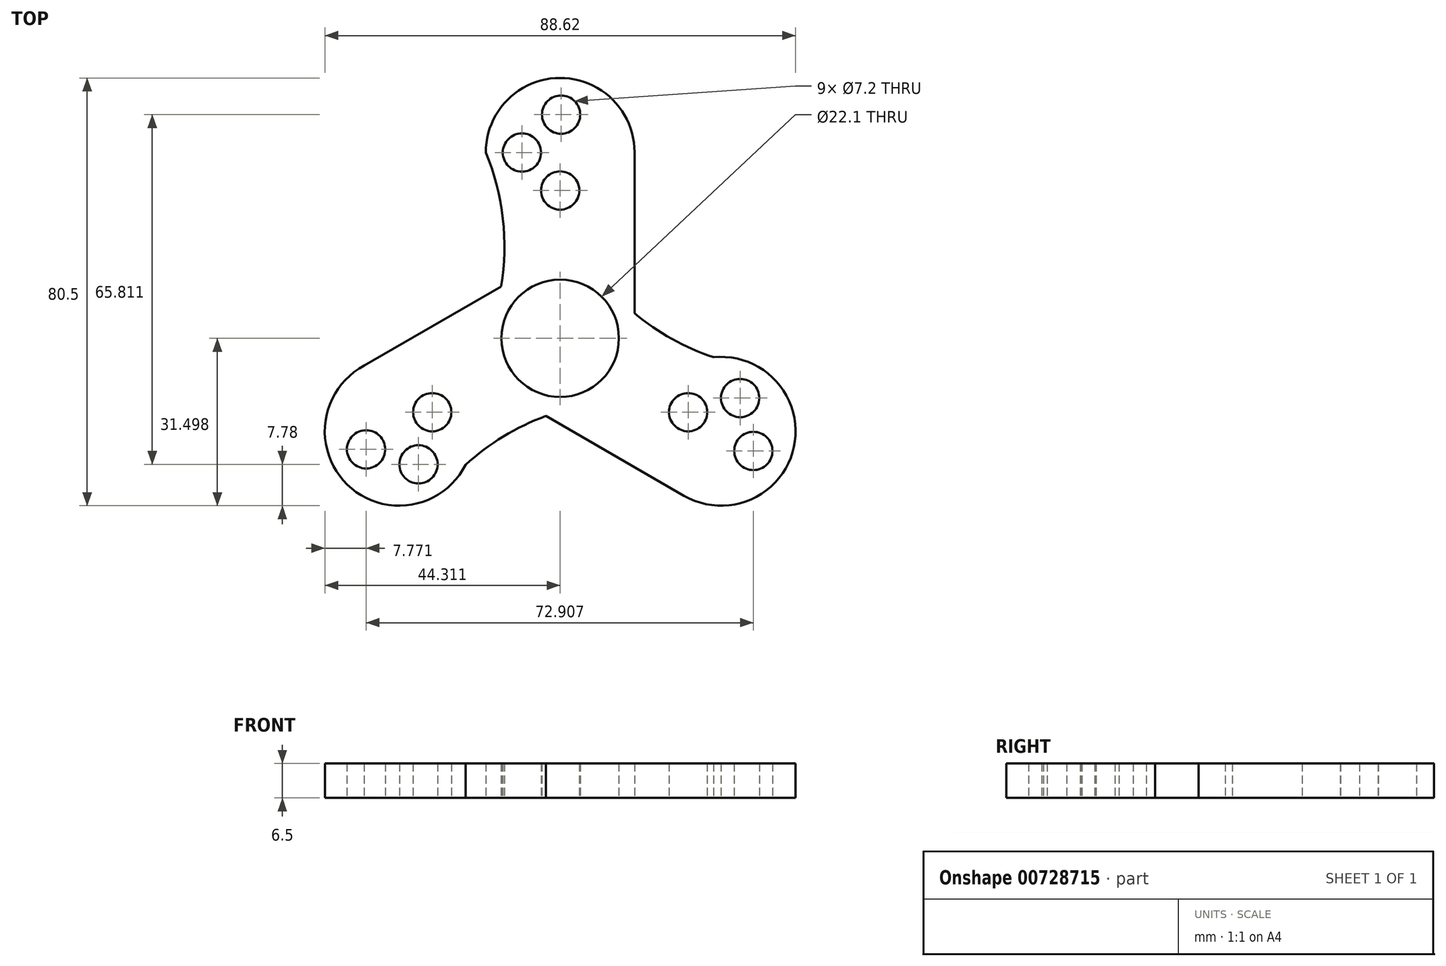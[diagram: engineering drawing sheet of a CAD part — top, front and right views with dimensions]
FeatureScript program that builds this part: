
annotation { "Feature Type Name" : "Feature", "Feature Type Description" : "" }
export const myFeature = defineFeature(function(context is Context, id is Id, definition is map)
    precondition{}
    {
        {
            var Q0;
            Q0=qCreatedBy(makeId("Top.planeOp"),FACE);
            var sketch = newSketch(context, id + "F0", { "sketchPlane" : qUnion([Q0])});
            skCircle(sketch, "E0", {"center": v(0.12, 0.22) * mm, "radius": 11.05 * mm});
            skCircle(sketch, "E1", {"center": v(0.12, 0.22) * mm, "radius": 14 * mm});
            skCircle(sketch, "E2", {"center": v(0.12, 35.22) * mm, "radius": 14 * mm});
            skCircle(sketch, "E3", {"center": v(0.3, 42.31) * mm, "radius": 3.6 * mm});
            skCircle(sketch, "E4", {"center": v(-7.08, 35.18) * mm, "radius": 3.6 * mm});
            skCircle(sketch, "E5.1.0", {"center": v(-30.2, -17.28) * mm, "radius": 14 * mm});
            skCircle(sketch, "E5.2.0", {"center": v(30.43, -17.28) * mm, "radius": 14 * mm});
            skCircle(sketch, "E6.1.0", {"center": v(-36.42, -20.68) * mm, "radius": 3.6 * mm});
            skCircle(sketch, "E6.2.0", {"center": v(36.49, -20.98) * mm, "radius": 3.6 * mm});
            skCircle(sketch, "E7.1.0", {"center": v(-26.55, -23.5) * mm, "radius": 3.6 * mm});
            skCircle(sketch, "E7.2.0", {"center": v(34, -11.02) * mm, "radius": 3.6 * mm});
            skCircle(sketch, "E8", {"center": v(0.12, 28.03) * mm, "radius": 3.6 * mm});
            skCircle(sketch, "E9.1.0", {"center": v(-23.97, -13.69) * mm, "radius": 3.6 * mm});
            skCircle(sketch, "E9.2.0", {"center": v(24.2, -13.69) * mm, "radius": 3.6 * mm});
            skArc(sketch, "E10", {"start": v(-18.8, -9.13) * mm, "mid": v(-10.67, 12.4) * mm, "end": v(-13.88, 35.18) * mm});
            skArc(sketch, "E11.1.0", {"start": v(17.59, -11.72) * mm, "mid": v(-5.12, -15.43) * mm, "end": v(-23.25, -29.6) * mm});
            skArc(sketch, "E11.2.0", {"start": v(1.63, 21.1) * mm, "mid": v(16.2, 3.28) * mm, "end": v(37.54, -5.33) * mm});
            skPoint(sketch, "E11.center", {"position": v(0.14, 0.08) * mm});
            skLineSegment(sketch, "E12", {"start": v(14.12, 35.22) * mm, "end": v(14.12, 0.22) * mm});
            skLineSegment(sketch, "E13.1.0", {"start": v(-37.56, -5.38) * mm, "end": v(-7.25, 12.12) * mm});
            skPoint(sketch, "E13.center", {"position": v(0, 0) * mm});
            skLineSegment(sketch, "E14", {"start": v(-6.58, -12.07) * mm, "end": v(23.43, -29.4) * mm});
            skSolve(sketch);
        }
        {
            var Q0;
            {var subQ0=sQuery(id+"F0.wireOp",EDGE,"E11.1.0");var subQ1=sQuery(id+"F0.wireOp",EDGE,"E5.1.0");var subQ2=makeQuery(id+"F0.imprint","INTERSECT",VERTEX,{"disambiguationData":[OD(0.0)],"derivedFrom":[subQ1,subQ0]});Q0=makeQuery(id+"F0.imprint","IMPRINT",FACE,{"disambiguationData":[TD([[makeQuery(id+"F0.imprint","IMPRINT",EDGE,{"disambiguationData":[TD([[subQ2,-1.0]])],"derivedFrom":subQ1}),1.0]])]});}
            var Q1;
            {var subQ0=sQuery(id+"F0.wireOp",EDGE,"E14");var subQ1=sQuery(id+"F0.wireOp",EDGE,"E1");var subQ2=makeQuery(id+"F0.imprint","INTERSECT",VERTEX,{"derivedFrom":[subQ1,subQ0]});Q1=makeQuery(id+"F0.imprint","IMPRINT",FACE,{"disambiguationData":[TD([[makeQuery(id+"F0.imprint","IMPRINT",EDGE,{"disambiguationData":[TD([[subQ2,-1.0]])],"derivedFrom":subQ1}),-1.0]])]});}
            var Q2;
            {var subQ0=sQuery(id+"F0.wireOp",EDGE,"E11.1.0");var subQ1=sQuery(id+"F0.wireOp",EDGE,"E1");var subQ2=makeQuery(id+"F0.imprint","INTERSECT",VERTEX,{"disambiguationData":[OD(0.0)],"derivedFrom":[subQ1,subQ0]});Q2=makeQuery(id+"F0.imprint","IMPRINT",FACE,{"disambiguationData":[TD([[makeQuery(id+"F0.imprint","IMPRINT",EDGE,{"disambiguationData":[TD([[subQ2,-1.0]])],"derivedFrom":subQ1}),1.0]])]});}
            var Q3;
            Q3=makeQuery(id+"F0.imprint","IMPRINT",FACE,{"disambiguationData":[TD([[makeQuery(id+"F0.imprint","IMPRINT",EDGE,{"derivedFrom":sQuery(id+"F0.wireOp",EDGE,"E6.2.0")}),-1.0]])]});
            var Q4;
            Q4=makeQuery(id+"F0.imprint","IMPRINT",FACE,{"disambiguationData":[TD([[makeQuery(id+"F0.imprint","IMPRINT",EDGE,{"derivedFrom":sQuery(id+"F0.wireOp",EDGE,"E6.1.0")}),-1.0]])]});
            var Q5;
            {var subQ0=sQuery(id+"F0.wireOp",EDGE,"E13.1.0");var subQ1=sQuery(id+"F0.wireOp",EDGE,"E1");var subQ2=makeQuery(id+"F0.imprint","INTERSECT",VERTEX,{"derivedFrom":[subQ1,subQ0]});Q5=makeQuery(id+"F0.imprint","IMPRINT",FACE,{"disambiguationData":[TD([[makeQuery(id+"F0.imprint","IMPRINT",EDGE,{"disambiguationData":[TD([[subQ2,-1.0]])],"derivedFrom":subQ1}),-1.0]])]});}
            var Q6;
            {var subQ0=sQuery(id+"F0.wireOp",EDGE,"E10");var subQ1=sQuery(id+"F0.wireOp",EDGE,"E1");var subQ2=makeQuery(id+"F0.imprint","INTERSECT",VERTEX,{"disambiguationData":[OD(0.0)],"derivedFrom":[subQ1,subQ0]});Q6=makeQuery(id+"F0.imprint","IMPRINT",FACE,{"disambiguationData":[TD([[makeQuery(id+"F0.imprint","IMPRINT",EDGE,{"disambiguationData":[TD([[subQ2,-1.0]])],"derivedFrom":subQ1}),1.0]])]});}
            var Q7;
            {var subQ0=sQuery(id+"F0.wireOp",EDGE,"E11.2.0");var subQ1=sQuery(id+"F0.wireOp",EDGE,"E1");var subQ2=makeQuery(id+"F0.imprint","INTERSECT",VERTEX,{"disambiguationData":[OD(0.0)],"derivedFrom":[subQ1,subQ0]});Q7=makeQuery(id+"F0.imprint","IMPRINT",FACE,{"disambiguationData":[TD([[makeQuery(id+"F0.imprint","IMPRINT",EDGE,{"disambiguationData":[TD([[subQ2,1.0]])],"derivedFrom":subQ1}),1.0]])]});}
            var Q8;
            {var subQ0=sQuery(id+"F0.wireOp",EDGE,"E12");var subQ1=sQuery(id+"F0.wireOp",EDGE,"E1");var subQ2=makeQuery(id+"F0.imprint","INTERSECT",VERTEX,{"derivedFrom":[subQ1,subQ0]});Q8=makeQuery(id+"F0.imprint","IMPRINT",FACE,{"disambiguationData":[TD([[makeQuery(id+"F0.imprint","IMPRINT",EDGE,{"disambiguationData":[TD([[subQ2,-1.0]])],"derivedFrom":subQ1}),-1.0]])]});}
            var Q9;
            {var subQ0=sQuery(id+"F0.wireOp",EDGE,"E10");var subQ1=sQuery(id+"F0.wireOp",EDGE,"E2");var subQ2=makeQuery(id+"F0.imprint","INTERSECT",VERTEX,{"disambiguationData":[OD(0.0)],"derivedFrom":[subQ1,subQ0]});Q9=makeQuery(id+"F0.imprint","IMPRINT",FACE,{"disambiguationData":[TD([[makeQuery(id+"F0.imprint","IMPRINT",EDGE,{"disambiguationData":[TD([[subQ2,-1.0]])],"derivedFrom":subQ1}),1.0]])]});}
            var Q10;
            Q10=makeQuery(id+"F0.imprint","IMPRINT",FACE,{"disambiguationData":[TD([[makeQuery(id+"F0.imprint","IMPRINT",EDGE,{"derivedFrom":sQuery(id+"F0.wireOp",EDGE,"599df940-7847-41b0-ac96-d3a5cff95a5d")}),-1.0]])]});
            var Q11;
            {var subQ5=sQuery(id+"F0.wireOp",EDGE,"E11.2.0");var subQ6=sQuery(id+"F0.wireOp",EDGE,"E1");var subQ7=makeQuery(id+"F0.imprint","INTERSECT",VERTEX,{"disambiguationData":[OD(0.0)],"derivedFrom":[subQ6,subQ5]});Q11=makeQuery(id+"F0.imprint","IMPRINT",FACE,{"disambiguationData":[TD([[makeQuery(id+"F0.imprint","IMPRINT",EDGE,{"disambiguationData":[TD([[subQ7,1.0]])],"derivedFrom":subQ6}),-1.0]])]});}
            var Q12;
            Q12=makeQuery(id+"F0.imprint","IMPRINT",FACE,{"disambiguationData":[TD([[makeQuery(id+"F0.imprint","IMPRINT",EDGE,{"derivedFrom":sQuery(id+"F0.wireOp",EDGE,"E0")}),-1.0]])]});
            var Q13;
            {var subQ1=sQuery(id+"F0.wireOp",EDGE,"E10");var subQ3=sQuery(id+"F0.wireOp",EDGE,"E1");var subQ4=makeQuery(id+"F0.imprint","INTERSECT",VERTEX,{"disambiguationData":[OD(0.0)],"derivedFrom":[subQ3,subQ1]});Q13=makeQuery(id+"F0.imprint","IMPRINT",FACE,{"disambiguationData":[TD([[makeQuery(id+"F0.imprint","IMPRINT",EDGE,{"disambiguationData":[TD([[subQ4,-1.0]])],"derivedFrom":subQ3}),-1.0]])]});}
            var Q14;
            {var subQ3=sQuery(id+"F0.wireOp",EDGE,"E14");var subQ7=sQuery(id+"F0.wireOp",EDGE,"E1");var subQ9=makeQuery(id+"F0.imprint","INTERSECT",VERTEX,{"derivedFrom":[subQ7,subQ3]});Q14=makeQuery(id+"F0.imprint","IMPRINT",FACE,{"disambiguationData":[TD([[makeQuery(id+"F0.imprint","IMPRINT",EDGE,{"disambiguationData":[TD([[subQ9,1.0]])],"derivedFrom":subQ7}),-1.0]])]});}
            var Q15;
            {var subQ1=sQuery(id+"F0.wireOp",EDGE,"E11.1.0");var subQ3=sQuery(id+"F0.wireOp",EDGE,"E1");var subQ4=makeQuery(id+"F0.imprint","INTERSECT",VERTEX,{"disambiguationData":[OD(0.0)],"derivedFrom":[subQ3,subQ1]});Q15=makeQuery(id+"F0.imprint","IMPRINT",FACE,{"disambiguationData":[TD([[makeQuery(id+"F0.imprint","IMPRINT",EDGE,{"disambiguationData":[TD([[subQ4,-1.0]])],"derivedFrom":subQ3}),-1.0]])]});}
            var Q16;
            {var subQ3=sQuery(id+"F0.wireOp",EDGE,"E1");var subQ7=sQuery(id+"F0.wireOp",EDGE,"E12");var subQ8=makeQuery(id+"F0.imprint","INTERSECT",VERTEX,{"derivedFrom":[subQ3,subQ7]});Q16=makeQuery(id+"F0.imprint","IMPRINT",FACE,{"disambiguationData":[TD([[makeQuery(id+"F0.imprint","IMPRINT",EDGE,{"disambiguationData":[TD([[subQ8,1.0]])],"derivedFrom":subQ3}),-1.0]])]});}
            var Q17;
            Q17=makeQuery(id+"F0.imprint","IMPRINT",FACE,{"disambiguationData":[TD([[makeQuery(id+"F0.imprint","IMPRINT",EDGE,{"derivedFrom":sQuery(id+"F0.wireOp",EDGE,"E3")}),-1.0]])]});
            extrude(context, id + "F1", {"entities" : qUnion([Q0, Q1, Q2, Q3, Q4, Q5, Q6, Q7, Q8, Q9, Q10, Q11, Q12, Q13, Q14, Q15, Q16, Q17]), "depth" : 6.5 * mm, "offsetDistance" : 25 * mm});
        }
    });
